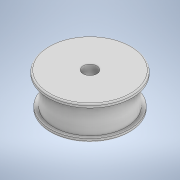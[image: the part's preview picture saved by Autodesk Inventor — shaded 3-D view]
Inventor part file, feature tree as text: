
AUTODESK INVENTOR PART (.ipt)
format: ipt  version: 2022 (Build 260153000, 153)  size: 140,288 bytes
history: native  units: in
note: dims shown in document units (in); Inventor stores cm internally (conversion verified against a paired STEP export)
features: revolve x1, sketch x1
ambient origin geometry x8: Origin, YZ Plane, XZ Plane, XY Plane, X Axis, Y Axis, Z Axis, Center Point
bodies: Solid1 (feature_tree)
feature tree (2):
  revolve  "Revolution1"  [1 undecoded]
  sketch  "Sketch1"  dims[d0=1.9685in d1=0.3937in d2=1.9685in d3=0.1969in d4=0.315in d5=1.5748in d6=0.1969in d7=1.8504in d8=0.0787in d9=90.0deg]
note: 1 required parameter value undecoded (feature->parameter linkage not recoverable at this tier; creation-order binding heuristic only, values carry confidence <= 0.55)
